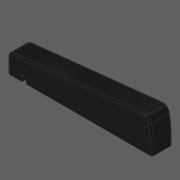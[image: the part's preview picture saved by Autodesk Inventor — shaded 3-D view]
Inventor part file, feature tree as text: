
AUTODESK INVENTOR PART (.ipt)
format: ipt  version: 2020 (Build 240168000, 168)  size: 253,952 bytes
history: native  units: in
note: dims shown in document units (in); Inventor stores cm internally (conversion verified against a paired STEP export)
features: other x3, extrude x3, fillet x2
ambient origin geometry x8: Origin, YZ Plane, XZ Plane, XY Plane, X Axis, Y Axis, Z Axis, Center Point
bodies: Solid1 (feature_tree)
feature tree (8):
  other  "Slot Start Plane"
  other  "Key Profile"
  extrude  "Key"  Depth=0.063in
  extrude  "Protrusion Cutout"  TaperAngle=0.0deg  [1 undecoded]
  fillet  "Front Fillet"  [1 undecoded]
  extrude  "Slot"  Depth=0.1181in
  fillet  "Edge Softening"  Radius=0.1374in
  other  "Slot Sketch"
note: 2 required parameter values undecoded (feature->parameter linkage not recoverable at this tier; creation-order binding heuristic only, values carry confidence <= 0.55)
